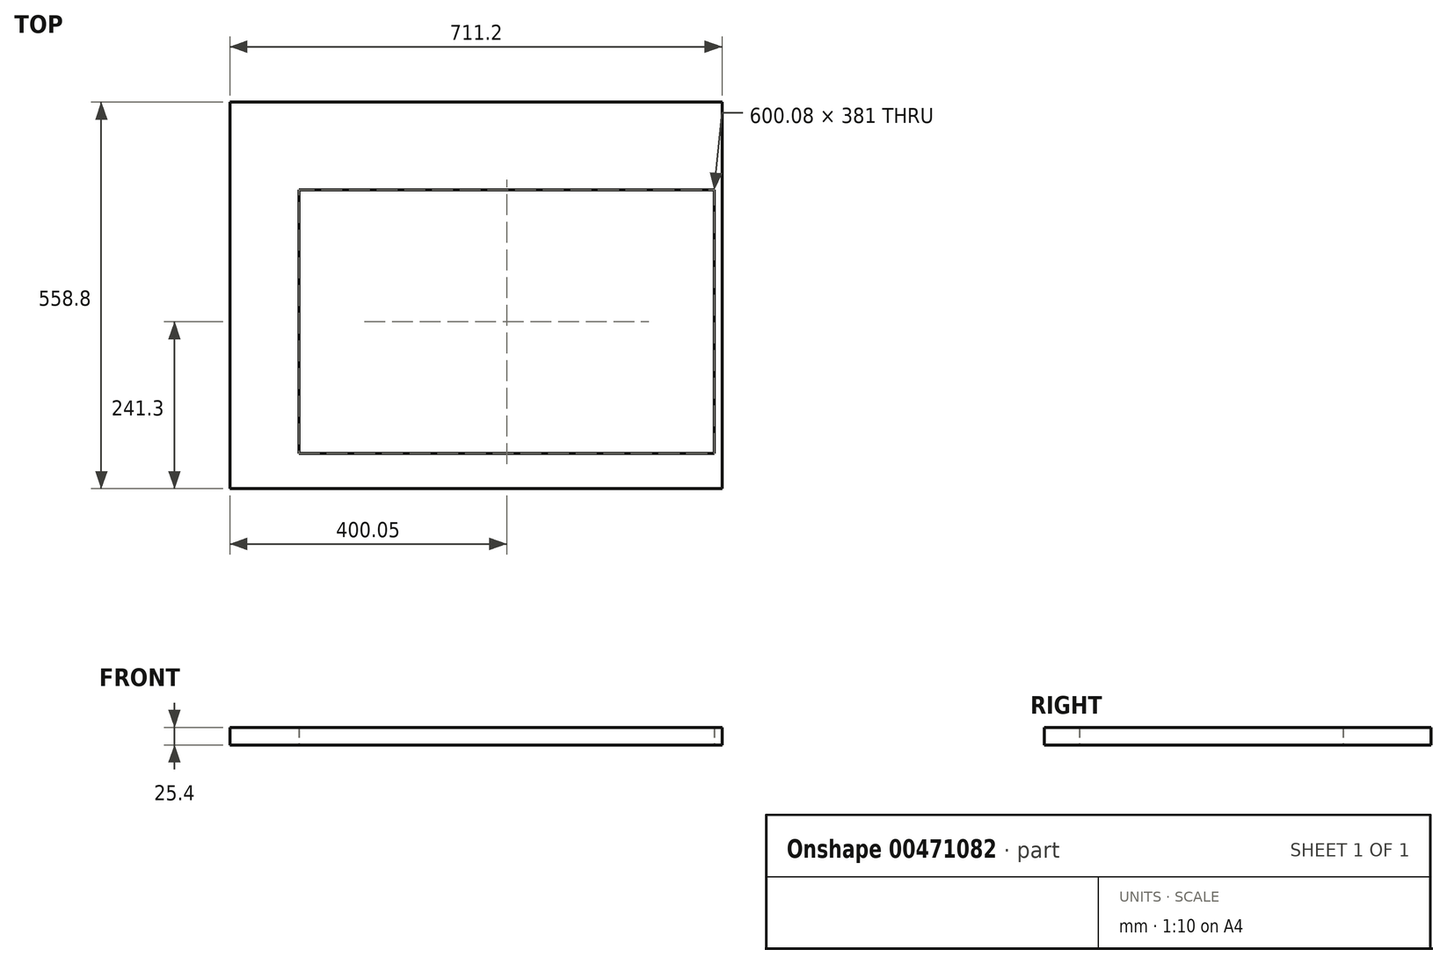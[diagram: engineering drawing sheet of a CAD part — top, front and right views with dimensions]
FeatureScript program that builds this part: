
annotation { "Feature Type Name" : "Feature", "Feature Type Description" : "" }
export const myFeature = defineFeature(function(context is Context, id is Id, definition is map)
    precondition{}
    {
        {
            var Q0;
            Q0=qCreatedBy(makeId("Top.planeOp"),FACE);
            var sketch = newSketch(context, id + "F0", { "sketchPlane" : qUnion([Q0])});
            skLineSegment(sketch, "E0.bottom", {"start": v(-355.6, 279.4) * mm, "end": v(355.6, 279.4) * mm});
            skLineSegment(sketch, "E0.top", {"start": v(-355.6, -279.4) * mm, "end": v(355.6, -279.4) * mm});
            skLineSegment(sketch, "E0.left", {"start": v(-355.6, 279.4) * mm, "end": v(-355.6, -279.4) * mm});
            skLineSegment(sketch, "E0.right", {"start": v(355.6, 279.4) * mm, "end": v(355.6, -279.4) * mm});
            skPoint(sketch, "E1", {"position": v(-355.6, 0) * mm});
            skPoint(sketch, "E2", {"position": v(0, 279.4) * mm});
            skLineSegment(sketch, "E3", {"start": v(-255.59, 279.4) * mm, "end": v(-255.59, -279.4) * mm});
            skLineSegment(sketch, "E4", {"start": v(-155.57, 279.4) * mm, "end": v(-155.58, -279.4) * mm});
            skLineSegment(sketch, "E5", {"start": v(-55.56, 279.4) * mm, "end": v(-55.56, -279.4) * mm});
            skLineSegment(sketch, "E6", {"start": v(44.45, 279.4) * mm, "end": v(44.45, -279.4) * mm});
            skLineSegment(sketch, "E7", {"start": v(144.46, 279.4) * mm, "end": v(144.46, -279.4) * mm});
            skLineSegment(sketch, "E8", {"start": v(244.48, 279.4) * mm, "end": v(244.47, -279.4) * mm});
            skLineSegment(sketch, "E9", {"start": v(344.49, 279.4) * mm, "end": v(344.49, -279.4) * mm});
            skLineSegment(sketch, "E10", {"start": v(-355.6, 152.4) * mm, "end": v(355.6, 152.4) * mm});
            skLineSegment(sketch, "E11", {"start": v(-355.6, 25.4) * mm, "end": v(355.6, 25.4) * mm});
            skLineSegment(sketch, "E12", {"start": v(-355.6, -101.6) * mm, "end": v(355.6, -101.6) * mm});
            skLineSegment(sketch, "E13", {"start": v(-355.6, -228.6) * mm, "end": v(355.6, -228.6) * mm});
            skSolve(sketch);
        }
        {
            var Q0;
            Q0 = qSketchRegion(id + "F0", true);
            extrude(context, id + "F1", {"entities" : qUnion([Q0]), "depth" : 25.4 * mm});
        }
    });
